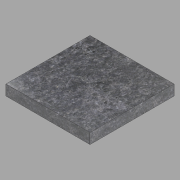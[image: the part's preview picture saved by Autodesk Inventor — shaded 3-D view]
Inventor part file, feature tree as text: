
AUTODESK INVENTOR PART (.ipt)
format: ipt  version: 2022.2 (Build 262287000, 287)  size: 110,592 bytes
history: native  units: in
note: dims shown in document units (in); Inventor stores cm internally (conversion verified against a paired STEP export)
features: extrude x1, sketch x1
ambient origin geometry x8: Origin, YZ Plane, XZ Plane, XY Plane, X Axis, Y Axis, Z Axis, Center Point
bodies: Solid1 (feature_tree)
feature tree (2):
  extrude  "Extrusion1"  Depth=16.0in
  sketch  "Sketch1"  dims[d0=16.0in d1=16.0in d2=2.0in d3=0.0in]
